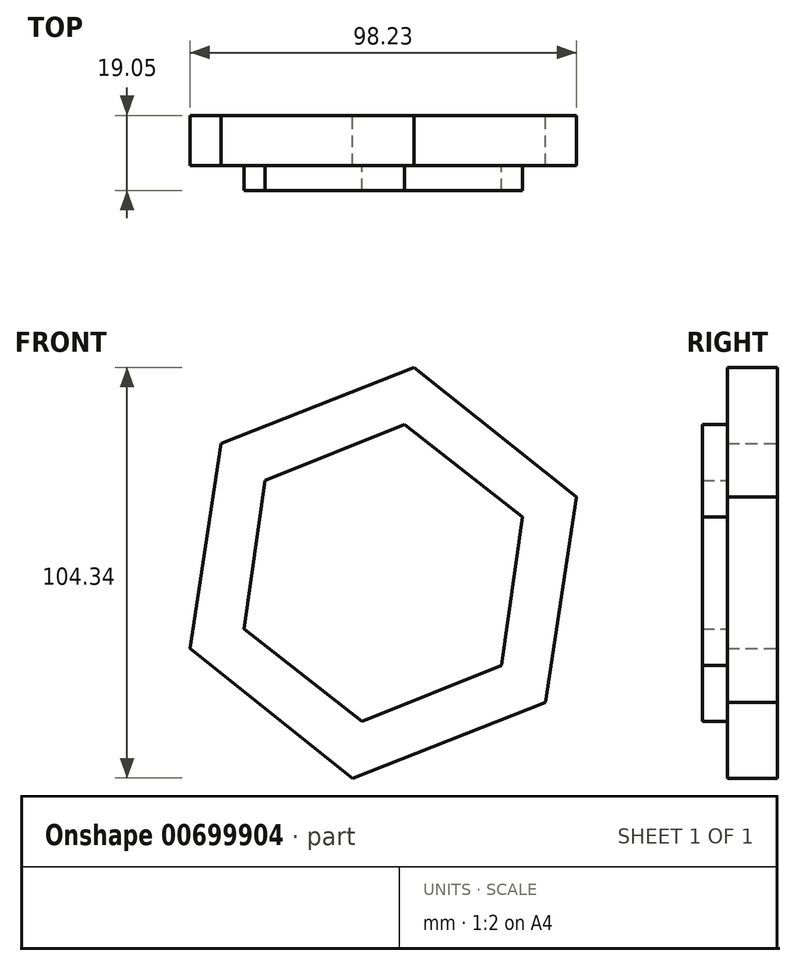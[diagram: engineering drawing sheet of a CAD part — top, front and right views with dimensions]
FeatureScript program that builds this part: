
annotation { "Feature Type Name" : "Feature", "Feature Type Description" : "" }
export const myFeature = defineFeature(function(context is Context, id is Id, definition is map)
    precondition{}
    {
        {
            var Q0;
            Q0=qCreatedBy(makeId("Front.planeOp"),FACE);
            var sketch = newSketch(context, id + "F0", { "sketchPlane" : qUnion([Q0])});
            skCircle(sketch, "E0.cCircle", {"center": v(-80.48, 43.8) * mm, "radius": 45.7 * mm, "construction": true});
            skLineSegment(sketch, "E0.0", {"start": v(-31.37, 63.07) * mm, "end": v(-39.23, 10.9) * mm});
            skLineSegment(sketch, "E0.1", {"start": v(-39.23, 10.9) * mm, "end": v(-88.35, -8.38) * mm});
            skLineSegment(sketch, "E0.2", {"start": v(-88.35, -8.38) * mm, "end": v(-129.6, 24.51) * mm});
            skLineSegment(sketch, "E0.3", {"start": v(-129.6, 24.51) * mm, "end": v(-121.74, 76.69) * mm});
            skLineSegment(sketch, "E0.4", {"start": v(-121.74, 76.69) * mm, "end": v(-72.62, 95.96) * mm});
            skLineSegment(sketch, "E0.5", {"start": v(-72.62, 95.96) * mm, "end": v(-31.37, 63.07) * mm});
            skPoint(sketch, "E0.0.midPoint", {"position": v(-35.3, 36.98) * mm});
            skSolve(sketch);
        }
        {
            var Q0;
            Q0 = qSketchRegion(id + "F0", true);
            extrude(context, id + "F1", {"entities" : qUnion([Q0]), "depth" : 12.7 * mm, "offsetDistance" : 25.4 * mm});
        }
        {
            var Q0;
            Q0=makeQuery(id+"F1.opExtrude","CAP_FACE",FACE,{"disambiguationData":[OSD([sQuery(id+"F0.wireOp",EDGE,"E0.0"),sQuery(id+"F0.wireOp",EDGE,"E0.1"),sQuery(id+"F0.wireOp",EDGE,"E0.2"),sQuery(id+"F0.wireOp",EDGE,"E0.3"),sQuery(id+"F0.wireOp",EDGE,"E0.4"),sQuery(id+"F0.wireOp",EDGE,"E0.5")])],"isStart":false});
            var sketch = newSketch(context, id + "F2", { "sketchPlane" : qUnion([Q0])});
            skCircle(sketch, "E1.cCircle", {"center": v(-80.48, 43.79) * mm, "radius": 33 * mm, "construction": true});
            skLineSegment(sketch, "E1.0", {"start": v(-50.49, 20.3) * mm, "end": v(-85.83, 6.07) * mm});
            skLineSegment(sketch, "E1.1", {"start": v(-85.83, 6.07) * mm, "end": v(-115.82, 29.56) * mm});
            skLineSegment(sketch, "E1.2", {"start": v(-115.82, 29.56) * mm, "end": v(-110.47, 67.28) * mm});
            skLineSegment(sketch, "E1.3", {"start": v(-110.47, 67.28) * mm, "end": v(-75.13, 81.51) * mm});
            skLineSegment(sketch, "E1.4", {"start": v(-75.13, 81.51) * mm, "end": v(-45.14, 58.02) * mm});
            skLineSegment(sketch, "E1.5", {"start": v(-45.14, 58.02) * mm, "end": v(-50.49, 20.3) * mm});
            skPoint(sketch, "E1.0.midPoint", {"position": v(-68.16, 13.18) * mm});
            skSolve(sketch);
        }
        {
            var Q0;
            Q0=makeQuery(id+"F2.imprint","IMPRINT",FACE,{"disambiguationData":[TD([[makeQuery(id+"F2.imprint","IMPRINT",EDGE,{"derivedFrom":sQuery(id+"F2.wireOp",EDGE,"E1.0")}),-1.0]])]});
            extrude(context, id + "F3", {"entities" : qUnion([Q0]), "operationType" : NewBodyOperationType.ADD, "depth" : 6.35 * mm, "offsetDistance" : 25.4 * mm});
        }
    });
